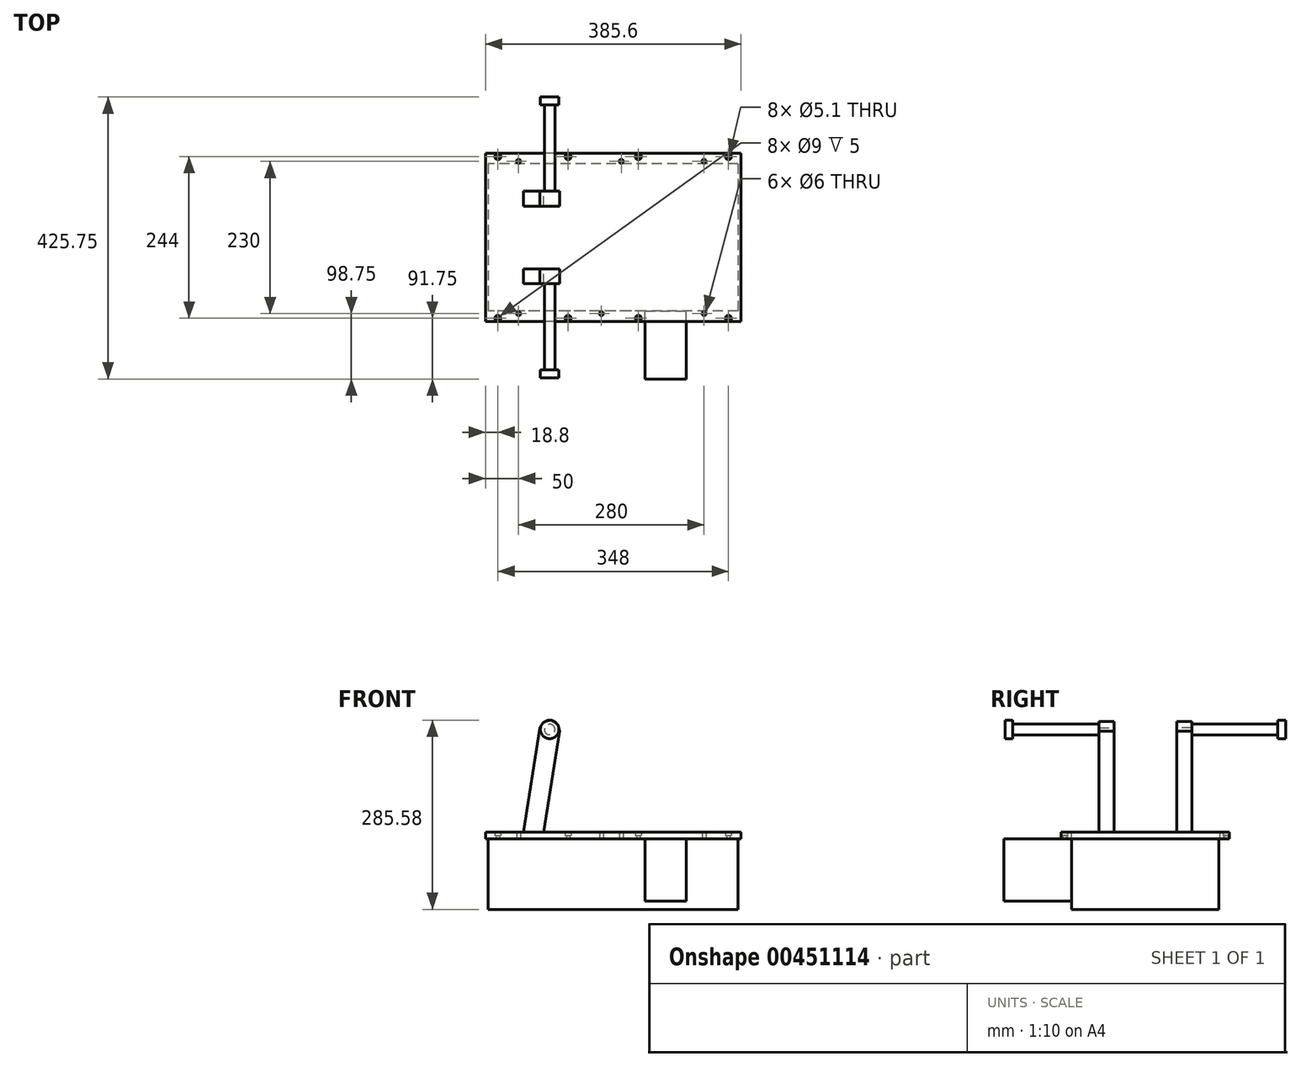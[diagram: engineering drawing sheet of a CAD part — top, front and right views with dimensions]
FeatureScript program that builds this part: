
annotation { "Feature Type Name" : "Feature", "Feature Type Description" : "" }
export const myFeature = defineFeature(function(context is Context, id is Id, definition is map)
    precondition{}
    {
        {
            var Q0;
            Q0=qCreatedBy(makeId("Top.planeOp"),FACE);
            var sketch = newSketch(context, id + "F0", { "sketchPlane" : qUnion([Q0])});
            skLineSegment(sketch, "E0.bottom", {"start": v(192.8, -127) * mm, "end": v(-192.8, -127) * mm});
            skLineSegment(sketch, "E0.top", {"start": v(192.8, 127) * mm, "end": v(-192.8, 127) * mm});
            skLineSegment(sketch, "E0.left", {"start": v(192.8, -127) * mm, "end": v(192.8, 127) * mm});
            skLineSegment(sketch, "E0.right", {"start": v(-192.8, -127) * mm, "end": v(-192.8, 127) * mm});
            skPoint(sketch, "E0.middle", {"position": v(0, 0) * mm});
            skSolve(sketch);
        }
        {
            var Q0;
            Q0=qSketchRegion(id+"F0",true);
            extrude(context, id + "F1", {"entities" : qUnion([Q0]), "depth" : 10 * mm});
        }
        {
            var Q0;
            Q0=makeQuery(id+"F1.opExtrude","CAP_FACE",FACE,{"disambiguationData":[OSD([sQuery(id+"F0.wireOp",EDGE,"E0.bottom"),sQuery(id+"F0.wireOp",EDGE,"E0.top"),sQuery(id+"F0.wireOp",EDGE,"E0.left"),sQuery(id+"F0.wireOp",EDGE,"E0.right")])],"isStart":true});
            var sketch = newSketch(context, id + "F2", { "sketchPlane" : qUnion([Q0])});
            skLineSegment(sketch, "E1.bottom", {"start": v(188.5, -111.15) * mm, "end": v(-188.5, -111.15) * mm});
            skLineSegment(sketch, "E1.top", {"start": v(188.5, 111.15) * mm, "end": v(-188.5, 111.15) * mm});
            skLineSegment(sketch, "E1.left", {"start": v(188.5, -111.15) * mm, "end": v(188.5, 111.15) * mm});
            skLineSegment(sketch, "E1.right", {"start": v(-188.5, -111.15) * mm, "end": v(-188.5, 111.15) * mm});
            skPoint(sketch, "E1.middle", {"position": v(0, 0) * mm});
            skSolve(sketch);
        }
        {
            var Q0;
            Q0=qSketchRegion(id+"F2",true);
            extrude(context, id + "F3", {"entities" : qUnion([Q0]), "operationType" : NewBodyOperationType.ADD, "depth" : 106.5 * mm});
        }
        {
            var Q0;
            {var subQ0=sQuery(id+"F0.wireOp",EDGE,"E0.left");var subQ1=sQuery(id+"F0.wireOp",EDGE,"E0.top");var subQ2=sQuery(id+"F0.wireOp",EDGE,"E0.right");var subQ3=sQuery(id+"F0.wireOp",EDGE,"E0.bottom");Q0=makeQuery(id+"FRL6UhUfdcv4TXD_1.boolean.opBoolean","SPLIT",FACE,{"disambiguationData":[TD([makeQuery(id+"F1.opExtrude","SWEPT_FACE",FACE,{"disambiguationData":[OSD([subQ3])]})])],"derivedFrom":makeQuery(id+"F1.opExtrude","CAP_FACE",FACE,{"disambiguationData":[OSD([subQ3,subQ1,subQ0,subQ2])],"isStart":false})});}
            var sketch = newSketch(context, id + "F4", { "sketchPlane" : qUnion([Q0])});
            skPoint(sketch, "E2", {"position": v(-142.8, 115) * mm});
            skPoint(sketch, "E3", {"position": v(12.2, 115) * mm});
            skPoint(sketch, "E4", {"position": v(137.2, 115) * mm});
            skPoint(sketch, "E5.MirrorP", {"position": v(137.2, -115) * mm});
            skPoint(sketch, "E6.MirrorP", {"position": v(-142.8, -115) * mm});
            skPoint(sketch, "E7", {"position": v(-17.8, -115) * mm});
            skPoint(sketch, "E8", {"position": v(-174, 122) * mm});
            skPoint(sketch, "E9", {"position": v(-68, 122) * mm});
            skPoint(sketch, "E10", {"position": v(38, 122) * mm});
            skPoint(sketch, "E11", {"position": v(174, 122) * mm});
            skPoint(sketch, "E12.MirrorP", {"position": v(174, -122) * mm});
            skPoint(sketch, "E13.MirrorP", {"position": v(38, -122) * mm});
            skPoint(sketch, "E14.MirrorP", {"position": v(-68, -122) * mm});
            skPoint(sketch, "E15.MirrorP", {"position": v(-174, -122) * mm});
            skSolve(sketch);
        }
        {
            var Q0;
            Q0=sQuery(id+"F4.wireOp",VERTEX,"E2");
            var Q1;
            Q1=sQuery(id+"F4.wireOp",VERTEX,"E3");
            var Q2;
            Q2=sQuery(id+"F4.wireOp",VERTEX,"E4");
            var Q3;
            Q3=sQuery(id+"F4.wireOp",VERTEX,"E5.MirrorP");
            var Q4;
            Q4=sQuery(id+"F4.wireOp",VERTEX,"E7");
            var Q5;
            Q5=sQuery(id+"F4.wireOp",VERTEX,"E6.MirrorP");
            var Q6;
            Q6=makeQuery(id+"F1.opExtrude","SWEPT_BODY",BODY,{"disambiguationData":[OSD([sQuery(id+"F0.wireOp",EDGE,"E0.bottom"),sQuery(id+"F0.wireOp",EDGE,"E0.top"),sQuery(id+"F0.wireOp",EDGE,"E0.left"),sQuery(id+"F0.wireOp",EDGE,"E0.right")])]});
            hole(context, id + "F5", {"style" : HoleStyle.SIMPLE, "endStyle" : HoleEndStyle.BLIND, "holeDiameter" : 6 * mm, "holeDepth" : 10 * mm, "tappedDepth" : 12 * mm, "tapClearance" : 3, "locations" : qUnion([Q0, Q1, Q2, Q3, Q4, Q5]), "scope" : qUnion([Q6])});
        }
        {
            var Q0;
            Q0=sQuery(id+"F4.wireOp",VERTEX,"E8");
            var Q1;
            Q1=sQuery(id+"F4.wireOp",VERTEX,"E9");
            var Q2;
            Q2=sQuery(id+"F4.wireOp",VERTEX,"E10");
            var Q3;
            Q3=sQuery(id+"F4.wireOp",VERTEX,"E11");
            var Q4;
            Q4=sQuery(id+"F4.wireOp",VERTEX,"E12.MirrorP");
            var Q5;
            Q5=sQuery(id+"F4.wireOp",VERTEX,"E13.MirrorP");
            var Q6;
            Q6=sQuery(id+"F4.wireOp",VERTEX,"E14.MirrorP");
            var Q7;
            Q7=sQuery(id+"F4.wireOp",VERTEX,"E15.MirrorP");
            var Q8;
            Q8=makeQuery(id+"F1.opExtrude","SWEPT_BODY",BODY,{"disambiguationData":[OSD([sQuery(id+"F0.wireOp",EDGE,"E0.bottom"),sQuery(id+"F0.wireOp",EDGE,"E0.top"),sQuery(id+"F0.wireOp",EDGE,"E0.left"),sQuery(id+"F0.wireOp",EDGE,"E0.right")])]});
            hole(context, id + "F6", {"style" : HoleStyle.C_BORE, "endStyle" : HoleEndStyle.BLIND, "holeDiameter" : 5.1 * mm, "cBoreDiameter" : 9 * mm, "cBoreDepth" : 5 * mm, "holeDepth" : 10 * mm, "tappedDepth" : 12 * mm, "tapClearance" : 3, "locations" : qUnion([Q0, Q1, Q2, Q3, Q4, Q5, Q6, Q7]), "scope" : qUnion([Q8])});
        }
        {
            var Q0;
            Q0=qCreatedBy(makeId("Front.planeOp"),FACE);
            cPlane(context, id + "F7", {"entities" : qUnion([Q0]), "cplaneType" : CPlaneType.OFFSET, "offset" : 47.45 * mm, "width" : 150 * mm, "height" : 150 * mm});
        }
        {
            var Q0;
            Q0=qCreatedBy(id+"F7.planeOp",FACE);
            var sketch = newSketch(context, id + "F8", { "sketchPlane" : qUnion([Q0])});
            skLineSegment(sketch, "E16", {"start": v(-95.82, 165.08) * mm, "end": v(-126.53, -28.83) * mm, "construction": true});
            skLineSegment(sketch, "E17", {"start": v(-110.63, 167.43) * mm, "end": v(-139.9, -17.39) * mm});
            skLineSegment(sketch, "E18", {"start": v(-81, 162.73) * mm, "end": v(-110.27, -22.08) * mm});
            skLineSegment(sketch, "E19", {"start": v(-110.63, 167.43) * mm, "end": v(-81, 162.73) * mm, "construction": true});
            skArc(sketch, "E20", {"start": v(-81, 162.73) * mm, "mid": v(-93.98, 176.7) * mm, "end": v(-110.63, 167.43) * mm});
            skLineSegment(sketch, "E21", {"start": v(-139.9, -17.39) * mm, "end": v(-110.27, -22.08) * mm});
            skCircle(sketch, "E22", {"center": v(-95.82, 165.08) * mm, "radius": 8 * mm, "construction": true});
            skSolve(sketch);
        }
        {
            var Q0;
            Q0 = qSketchRegion(id + "F8", true);
            extrude(context, id + "F9", {"entities" : qUnion([Q0]), "depth" : 22.55 * mm});
        }
        {
            var Q0;
            Q0=makeQuery(id+"F8.imprint","IMPRINT",FACE,{"disambiguationData":[TD([[makeQuery(id+"F8.imprint","IMPRINT",EDGE,{"derivedFrom":sQuery(id+"F8.wireOp",EDGE,"E17")}),1.0]])]});
            var sketch = newSketch(context, id + "F10", { "sketchPlane" : qUnion([Q0])});
            skCircle(sketch, "E23", {"center": v(-95.82, 165.08) * mm, "radius": 8 * mm});
            skSolve(sketch);
        }
        {
            var Q0;
            Q0 = qSketchRegion(id + "F10", true);
            extrude(context, id + "F11", {"entities" : qUnion([Q0]), "operationType" : NewBodyOperationType.ADD, "depth" : 164.55 * mm});
        }
        {
            var Q0;
            Q0=makeQuery(id+"F11.opExtrude","CAP_FACE",FACE,{"disambiguationData":[OSD([sQuery(id+"F10.wireOp",EDGE,"E23")])],"isStart":false});
            var sketch = newSketch(context, id + "F12", { "sketchPlane" : qUnion([Q0])});
            skCircle(sketch, "E24", {"center": v(-95.82, 165.08) * mm, "radius": 14 * mm});
            skSolve(sketch);
        }
        {
            var Q0;
            Q0 = qSketchRegion(id + "F12", true);
            extrude(context, id + "F13", {"entities" : qUnion([Q0]), "operationType" : NewBodyOperationType.ADD, "oppositeDirection" : true, "depth" : 12 * mm});
        }
        {
            var Q0;
            Q0=makeQuery(id+"F9.opExtrude","SWEPT_BODY",BODY,{"disambiguationData":[OSD([sQuery(id+"F8.wireOp",EDGE,"E17"),sQuery(id+"F8.wireOp",EDGE,"E18"),sQuery(id+"F8.wireOp",EDGE,"E20"),sQuery(id+"F8.wireOp",EDGE,"E21")])]});
            var Q1;
            Q1=qCreatedBy(makeId("Front.planeOp"),FACE);
            mirror(context, id + "F14", {"operationType" : NewBodyOperationType.ADD, "entities" : qUnion([Q0]), "mirrorPlane" : qUnion([Q1])});
        }
        {
            var Q0;
            Q0=makeQuery(id+"F3.opExtrude","SWEPT_FACE",FACE,{"disambiguationData":[OSD([sQuery(id+"F2.wireOp",EDGE,"E1.top")])]});
            var sketch = newSketch(context, id + "F15", { "sketchPlane" : qUnion([Q0])});
            skLineSegment(sketch, "E25.bottom", {"start": v(48, 0) * mm, "end": v(110, 0) * mm});
            skLineSegment(sketch, "E25.top", {"start": v(48, -94.2) * mm, "end": v(110, -94.2) * mm});
            skLineSegment(sketch, "E25.left", {"start": v(48, 0) * mm, "end": v(48, -94.2) * mm});
            skLineSegment(sketch, "E25.right", {"start": v(110, 0) * mm, "end": v(110, -94.2) * mm});
            skSolve(sketch);
        }
        {
            var Q0;
            Q0 = qSketchRegion(id + "F15", true);
            extrude(context, id + "F16", {"entities" : qUnion([Q0]), "operationType" : NewBodyOperationType.ADD, "depth" : 102.6 * mm, "offsetDistance" : 25 * mm});
        }
    });
